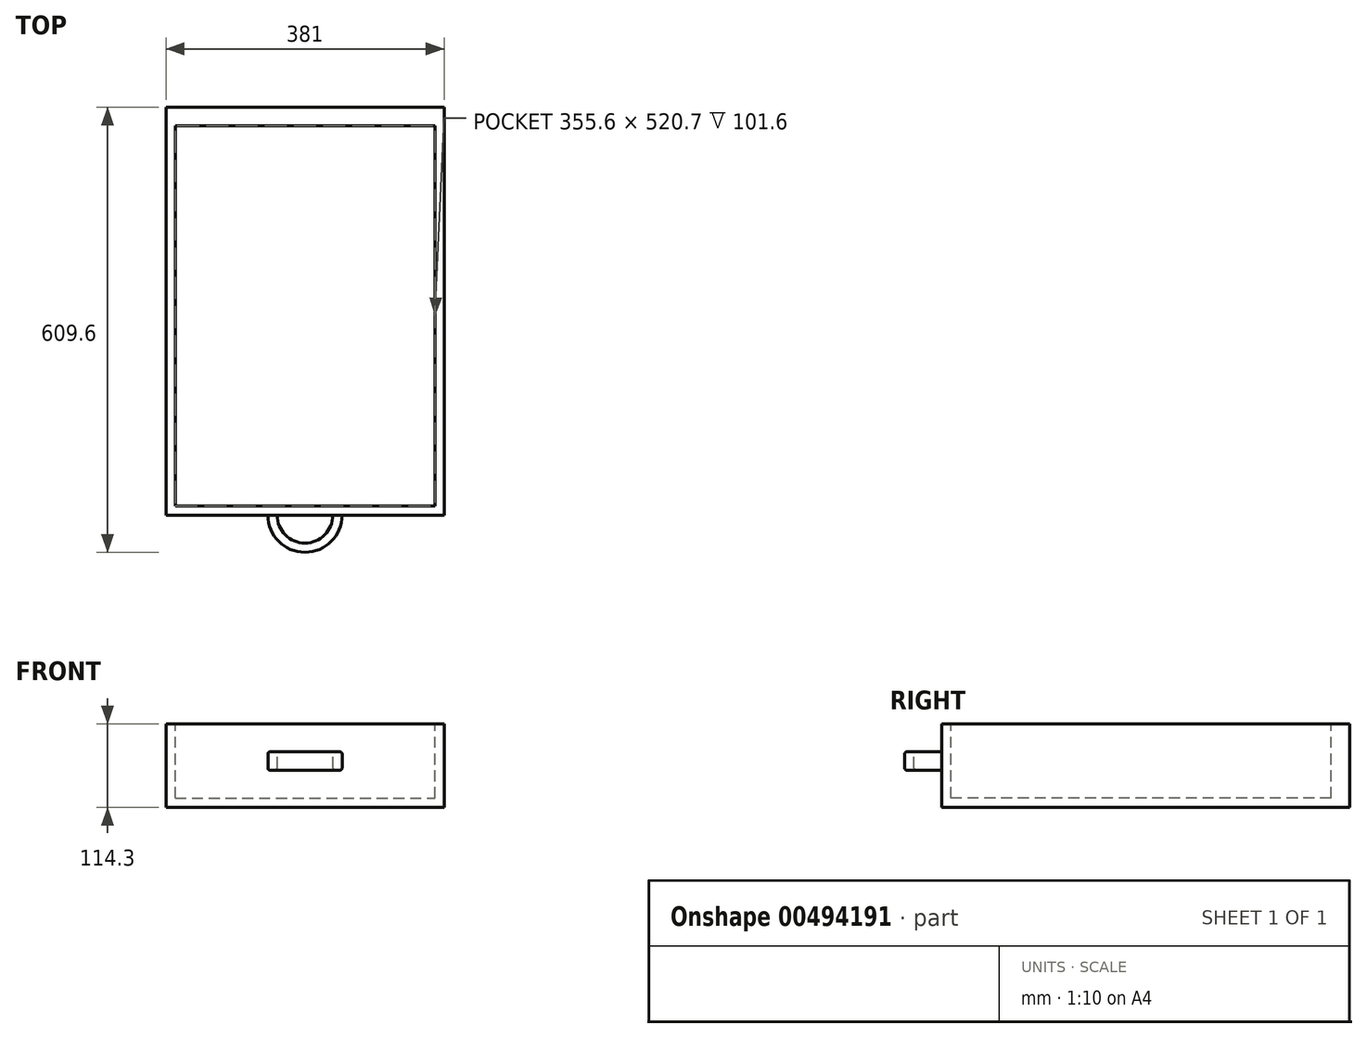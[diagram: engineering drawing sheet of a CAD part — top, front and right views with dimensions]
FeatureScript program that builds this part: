
annotation { "Feature Type Name" : "Feature", "Feature Type Description" : "" }
export const myFeature = defineFeature(function(context is Context, id is Id, definition is map)
    precondition{}
    {
        {
            var Q0;
            Q0=qCreatedBy(makeId("Front.planeOp"),FACE);
            var sketch = newSketch(context, id + "F0", { "sketchPlane" : qUnion([Q0])});
            skLineSegment(sketch, "E0.bottom", {"start": v(-33.41, 96.1) * mm, "end": v(347.59, 96.1) * mm});
            skLineSegment(sketch, "E0.top", {"start": v(-33.41, -18.2) * mm, "end": v(347.59, -18.2) * mm});
            skLineSegment(sketch, "E0.left", {"start": v(-33.41, 96.1) * mm, "end": v(-33.41, -18.2) * mm});
            skLineSegment(sketch, "E0.right", {"start": v(347.59, 96.1) * mm, "end": v(347.59, -18.2) * mm});
            skSolve(sketch);
        }
        {
            var Q0;
            Q0=qSketchRegion(id+"F0",true);
            var Q1;
            Q1 = qSketchRegion(id + "F2", true);
            extrude(context, id + "F1", {"entities" : qUnion([Q0, Q1]), "oppositeDirection" : true, "depth" : 558.8 * mm});
        }
        {
            var Q0;
            Q0=makeQuery(id+"F1.opExtrude","SWEPT_FACE",FACE,{"disambiguationData":[OSD([sQuery(id+"F0.wireOp",EDGE,"E0.bottom")])]});
            var sketch = newSketch(context, id + "F2", { "sketchPlane" : qUnion([Q0])});
            skLineSegment(sketch, "E1.bottom", {"start": v(-20.71, 533.4) * mm, "end": v(334.89, 533.4) * mm});
            skLineSegment(sketch, "E1.top", {"start": v(-20.71, 12.7) * mm, "end": v(334.89, 12.7) * mm});
            skLineSegment(sketch, "E1.left", {"start": v(-20.71, 533.4) * mm, "end": v(-20.71, 12.7) * mm});
            skLineSegment(sketch, "E1.right", {"start": v(334.89, 533.4) * mm, "end": v(334.89, 12.7) * mm});
            skSolve(sketch);
        }
        {
            var Q0;
            Q0=makeQuery(id+"F2.imprint","IMPRINT",FACE,{"disambiguationData":[TD([[makeQuery(id+"F2.imprint","IMPRINT",EDGE,{"derivedFrom":sQuery(id+"F2.wireOp",EDGE,"E1.bottom")}),-1.0]])]});
            extrude(context, id + "F3", {"entities" : qUnion([Q0]), "operationType" : NewBodyOperationType.REMOVE, "oppositeDirection" : true, "depth" : 101.6 * mm});
        }
        {
            var Q0;
            Q0=makeQuery(id+"F1.opExtrude","CAP_FACE",FACE,{"disambiguationData":[OSD([sQuery(id+"F0.wireOp",EDGE,"E0.bottom"),sQuery(id+"F0.wireOp",EDGE,"E0.top"),sQuery(id+"F0.wireOp",EDGE,"E0.left"),sQuery(id+"F0.wireOp",EDGE,"E0.right")])],"isStart":true});
            var sketch = newSketch(context, id + "F4", { "sketchPlane" : qUnion([Q0])});
            skLineSegment(sketch, "E2.bottom", {"start": v(106.29, 58) * mm, "end": v(207.89, 58) * mm});
            skLineSegment(sketch, "E2.top", {"start": v(106.29, 32.6) * mm, "end": v(207.89, 32.6) * mm});
            skLineSegment(sketch, "E2.left", {"start": v(106.29, 58) * mm, "end": v(106.29, 32.6) * mm});
            skLineSegment(sketch, "E2.right", {"start": v(207.89, 58) * mm, "end": v(207.89, 32.6) * mm});
            skLineSegment(sketch, "E3", {"start": v(106.29, 45.3) * mm, "end": v(207.89, 45.3) * mm});
            skLineSegment(sketch, "E4", {"start": v(157.09, 58) * mm, "end": v(157.09, 32.6) * mm});
            skSolve(sketch);
        }
        {
            var Q0;
            {var subQ3=sQuery(id+"F4.wireOp",EDGE,"E2.bottom");var subQ5=sQuery(id+"F4.wireOp",EDGE,"E2.left");var subQ7=makeQuery(id+"F4.imprint","INTERSECT",VERTEX,{"derivedFrom":[subQ3,subQ5]});Q0=makeQuery(id+"F4.imprint","IMPRINT",FACE,{"disambiguationData":[TD([[makeQuery(id+"F4.imprint","IMPRINT",EDGE,{"disambiguationData":[TD([[subQ7,-1.0]])],"derivedFrom":subQ3}),-1.0]])]});}
            var Q1;
            {var subQ3=sQuery(id+"F4.wireOp",EDGE,"E2.top");var subQ5=sQuery(id+"F4.wireOp",EDGE,"E2.left");var subQ7=makeQuery(id+"F4.imprint","INTERSECT",VERTEX,{"derivedFrom":[subQ3,subQ5]});Q1=makeQuery(id+"F4.imprint","IMPRINT",FACE,{"disambiguationData":[TD([[makeQuery(id+"F4.imprint","IMPRINT",EDGE,{"disambiguationData":[TD([[subQ7,-1.0]])],"derivedFrom":subQ3}),1.0]])]});}
            var Q2;
            Q2=sQuery(id+"F4.wireOp",EDGE,"E4");
            revolve(context, id + "F5", {"operationType" : NewBodyOperationType.ADD, "entities" : qUnion([Q0, Q1]), "axis" : qUnion([Q2]), "revolveType" : RevolveType.ONE_DIRECTION, "oppositeDirection" : true, "angle" : 180 * degree});
        }
        {
            var Q0;
            Q0=makeQuery(id+"F5.opRevolve","SWEPT_FACE",FACE,{"disambiguationData":[OSD([sQuery(id+"F4.wireOp",EDGE,"E2.bottom")])]});
            var sketch = newSketch(context, id + "F6", { "sketchPlane" : qUnion([Q0])});
            skLineSegment(sketch, "E5", {"start": v(118.99, 0) * mm, "end": v(195.19, 0) * mm});
            skArc(sketch, "E6", {"start": v(118.99, 0) * mm, "mid": v(157.09, -38.1) * mm, "end": v(195.19, 0) * mm});
            skSolve(sketch);
        }
        {
            var Q0;
            Q0=makeQuery(id+"F6.imprint","IMPRINT",FACE,{"disambiguationData":[TD([[makeQuery(id+"F6.imprint","IMPRINT",EDGE,{"derivedFrom":sQuery(id+"F6.wireOp",EDGE,"E5")}),1.0]])]});
            extrude(context, id + "F7", {"entities" : qUnion([Q0]), "operationType" : NewBodyOperationType.REMOVE, "endBound" : BoundingType.THROUGH_ALL, "oppositeDirection" : true, "depth" : 25.4 * mm});
        }
        {
            var Q0;
            Q0=makeQuery(id+"F5.opRevolve","SWEPT_EDGE",EDGE,{"disambiguationData":[OSD([sQuery(id+"F4.wireOp",EDGE,"E2.bottom"),sQuery(id+"F4.wireOp",EDGE,"E2.left")])]});
            var Q1;
            Q1=makeQuery(id+"F7.boolean.opBoolean","COPY",EDGE,{"derivedFrom":makeQuery(id+"F7.opExtrude","CAP_EDGE",EDGE,{"disambiguationData":[OSD([sQuery(id+"F6.wireOp",EDGE,"E6")])],"isStart":true})});
            var Q2;
            Q2=makeQuery(id+"F5.opRevolve","SWEPT_EDGE",EDGE,{"disambiguationData":[OSD([sQuery(id+"F4.wireOp",EDGE,"E2.top"),sQuery(id+"F4.wireOp",EDGE,"E2.left")])]});
            var Q3;
            Q3=makeQuery(id+"F7.boolean.opBoolean","INTERSECT",EDGE,{"derivedFrom":[makeQuery(id+"F5.opRevolve","SWEPT_FACE",FACE,{"disambiguationData":[OSD([sQuery(id+"F4.wireOp",EDGE,"E2.top")])]}),makeQuery(id+"F7.opExtrude","SWEPT_FACE",FACE,{"disambiguationData":[OSD([sQuery(id+"F6.wireOp",EDGE,"E6")])]})]});
            fillet(context, id + "F8", {"entities" : qUnion([Q0, Q1, Q2, Q3]), "radius" : 3.17 * mm, "tangentPropagation" : true, "allowEdgeOverflow" : false});
        }
    });
